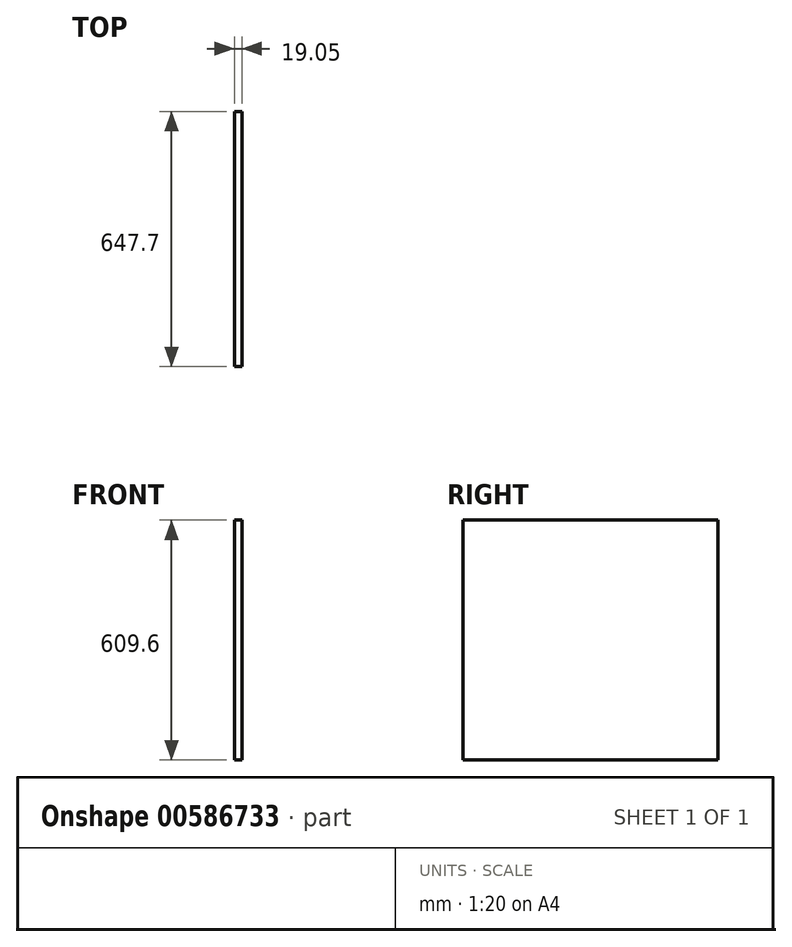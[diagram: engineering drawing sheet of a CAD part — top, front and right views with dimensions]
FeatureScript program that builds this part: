
annotation { "Feature Type Name" : "Feature", "Feature Type Description" : "" }
export const myFeature = defineFeature(function(context is Context, id is Id, definition is map)
    precondition{}
    {
        {
            var Q0;
            Q0=qCreatedBy(makeId("Right.planeOp"),FACE);
            var sketch = newSketch(context, id + "F0", { "sketchPlane" : qUnion([Q0])});
            skLineSegment(sketch, "E0.bottom", {"start": v(-394.88, 298.9) * mm, "end": v(252.82, 298.9) * mm});
            skLineSegment(sketch, "E0.top", {"start": v(-394.88, -310.7) * mm, "end": v(252.82, -310.7) * mm});
            skLineSegment(sketch, "E0.left", {"start": v(-394.88, 298.9) * mm, "end": v(-394.88, -310.7) * mm});
            skLineSegment(sketch, "E0.right", {"start": v(252.82, 298.9) * mm, "end": v(252.82, -310.7) * mm});
            skSolve(sketch);
        }
        {
            var Q0;
            Q0 = qSketchRegion(id + "F0", true);
            extrude(context, id + "F1", {"entities" : qUnion([Q0]), "depth" : 19.05 * mm, "offsetDistance" : 25.4 * mm});
        }
    });
